# Revit family: Check_Valves-Integral-McGuire-LFCK02
name_source: partatom
category: Plumbing Fixtures
revit_build: Autodesk Revit 2018 (Build: 20170223_1515(x64)
units: mm (PartAtom-declared; Revit-internal decimal feet)

## family parameters
Cut with Voids When Loaded = No
Host = Face
OmniClass Number = 23.45.55.11
OmniClass Title = Sanitary Components
Part Type = Normal
Room Calculation Point = No
Round Connector Dimension = Use Radius
Shared = Yes

## types (1)
- LFCK02
    Assembly Code = D2020300
    CW Connection = Yes
    CWFU = 1.5
    Default Elevation = 0"
    Description = LFCK02: 1/2 IPS X 3/8 OD
    HW Connection = Yes
    HWFU = 1.5
    Height = 1 3/16"
    IAPMO Compliance = cUPC Low Lead
    Inlet Diameter = 1/2"
    Inlet Radius = 1/4"
    Length = 1 1/2"
    Manufacturer = McGuire Manufacturing
    Material = Brass-McGuire-Low Lead-Chrome Plated
    Model = LFCK02
    Outlet Diameter = 3/8"
    Outlet Radius = 3/16"
    Price = Prices may vary. Please consult Manufacturer Representative for most up-to-date price list.
    Product Documentation Link = https://d163axztg8am2h.cloudfront.net
    Product Page URL = https://www.mcguiremfg.com
    URL = http://www.mcguiremfg.com
    Vent Connection = No
    WFU = 0
    Warranty Information = 15 Year Limited Warranty
    Waste Connection = No

## geometry (parser evidence)
native form markers: Sweep x3
no freeform markers — native parametric forms only
